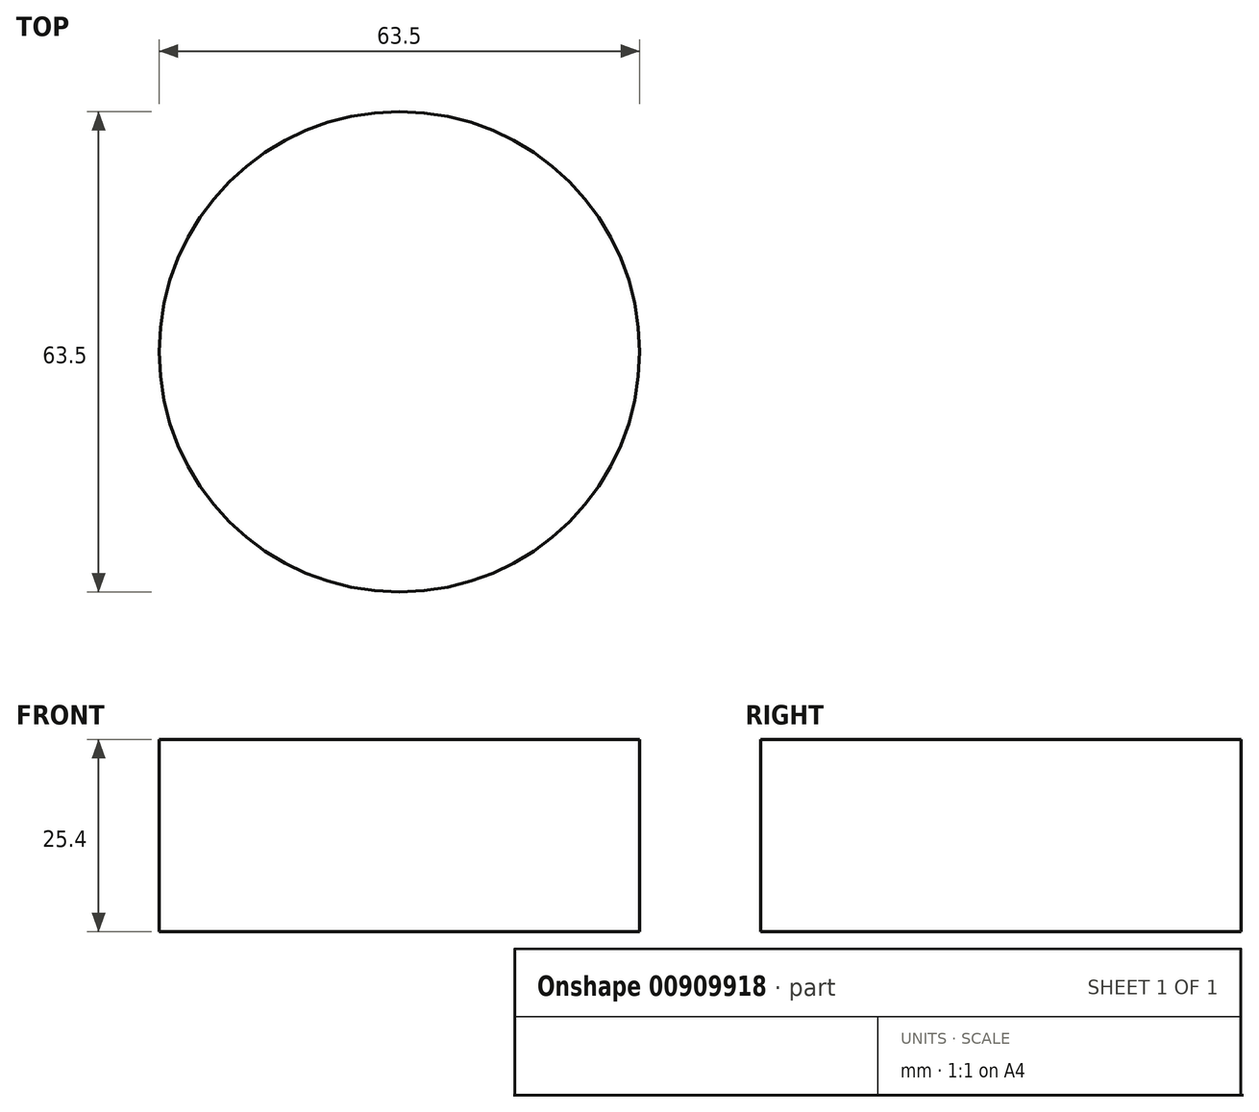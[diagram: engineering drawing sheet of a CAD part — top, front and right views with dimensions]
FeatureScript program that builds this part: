
annotation { "Feature Type Name" : "Feature", "Feature Type Description" : "" }
export const myFeature = defineFeature(function(context is Context, id is Id, definition is map)
    precondition{}
    {
        {
            var Q0;
            Q0=qCreatedBy(makeId("Top.planeOp"),FACE);
            var sketch = newSketch(context, id + "F0", { "sketchPlane" : qUnion([Q0])});
            skCircle(sketch, "E0", {"center": v(0, 0) * mm, "radius": 31.75 * mm});
            skSolve(sketch);
        }
        {
            var Q0;
            Q0=makeQuery(id+"F0.imprint","IMPRINT",FACE,{"disambiguationData":[TD([[makeQuery(id+"F0.imprint","IMPRINT",EDGE,{"derivedFrom":sQuery(id+"F0.wireOp",EDGE,"E0")}),1.0]])]});
            extrude(context, id + "F1", {"entities" : qUnion([Q0]), "depth" : 25.4 * mm, "offsetDistance" : 25.4 * mm});
        }
    });
